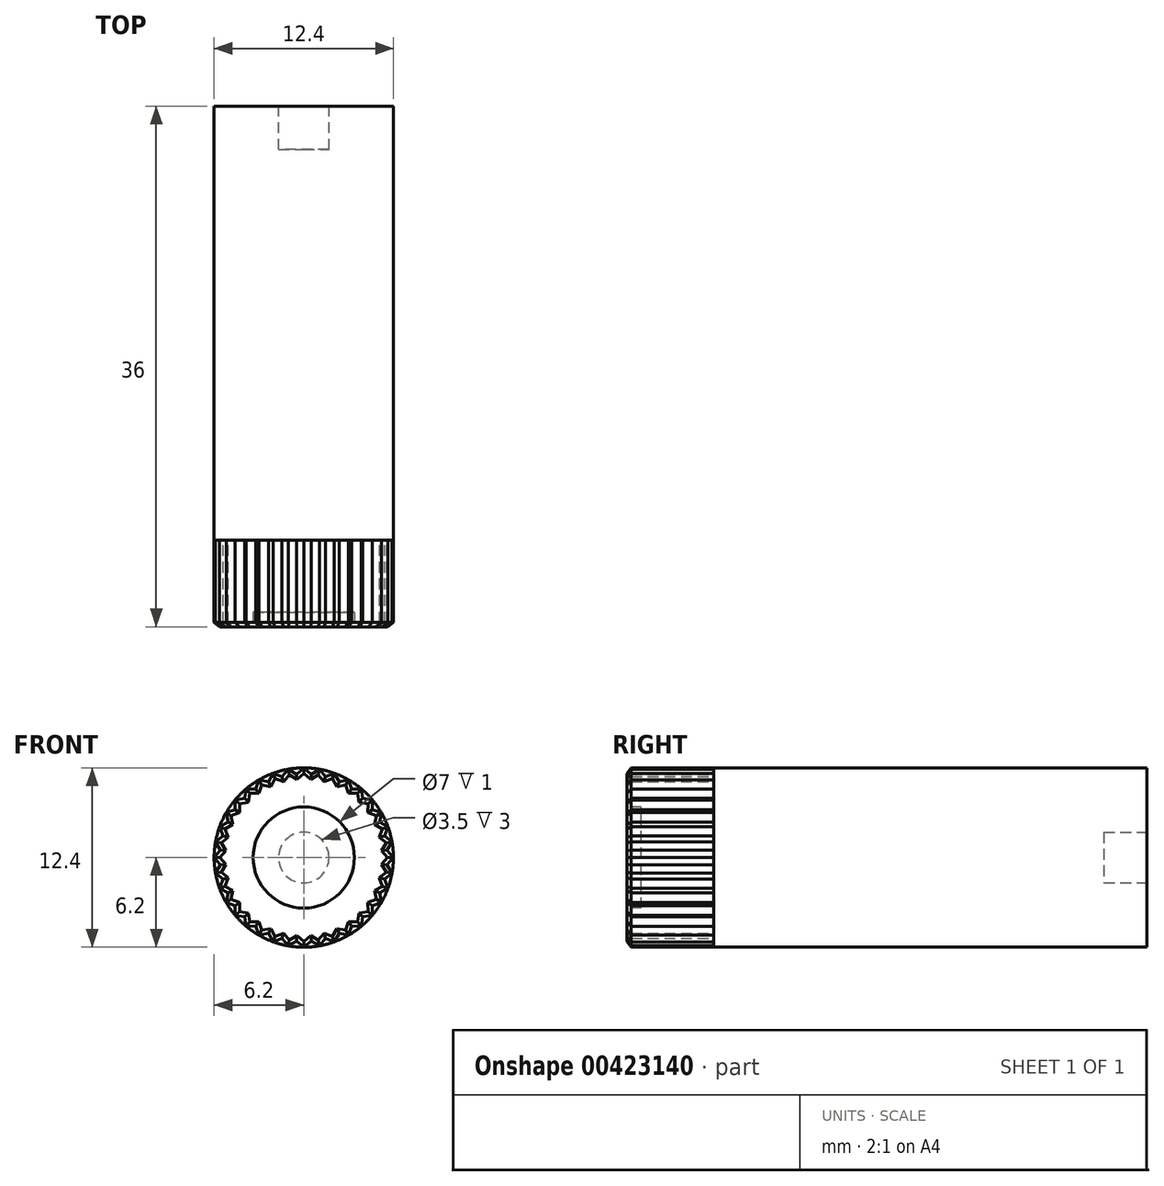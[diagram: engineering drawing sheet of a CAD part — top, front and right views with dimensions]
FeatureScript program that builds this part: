
annotation { "Feature Type Name" : "Feature", "Feature Type Description" : "" }
export const myFeature = defineFeature(function(context is Context, id is Id, definition is map)
    precondition{}
    {
        {
            var Q0;
            Q0=qCreatedBy(makeId("Front.planeOp"),FACE);
            var sketch = newSketch(context, id + "F0", { "sketchPlane" : qUnion([Q0])});
            skCircle(sketch, "E0", {"center": v(0, 0) * mm, "radius": 6.2 * mm});
            skSolve(sketch);
        }
        {
            var Q0;
            Q0 = qSketchRegion(id + "F0", true);
            extrude(context, id + "F1", {"entities" : qUnion([Q0]), "depth" : 30 * mm});
        }
        {
            var Q0;
            Q0=makeQuery(id+"F1.opExtrude","CAP_FACE",FACE,{"disambiguationData":[OSD([sQuery(id+"F0.wireOp",EDGE,"E0")])],"isStart":false});
            var sketch = newSketch(context, id + "F2", { "sketchPlane" : qUnion([Q0])});
            skLineSegment(sketch, "E1", {"start": v(6.2, 0) * mm, "end": v(5.76, 0.5) * mm});
            skLineSegment(sketch, "E2.MirrorCS", {"start": v(6.2, 0) * mm, "end": v(5.76, -0.5) * mm});
            skLineSegment(sketch, "E3.1.0", {"start": v(6.1, 1.08) * mm, "end": v(5.59, 1.5) * mm});
            skLineSegment(sketch, "E3.1.1", {"start": v(6.1, 1.08) * mm, "end": v(5.76, 0.5) * mm});
            skLineSegment(sketch, "E3.2.0", {"start": v(5.83, 2.12) * mm, "end": v(5.24, 2.44) * mm});
            skLineSegment(sketch, "E3.2.1", {"start": v(5.83, 2.12) * mm, "end": v(5.59, 1.5) * mm});
            skLineSegment(sketch, "E3.3.0", {"start": v(5.37, 3.1) * mm, "end": v(4.74, 3.32) * mm});
            skLineSegment(sketch, "E3.3.1", {"start": v(5.37, 3.1) * mm, "end": v(5.24, 2.44) * mm});
            skLineSegment(sketch, "E3.4.0", {"start": v(4.75, 3.99) * mm, "end": v(4.09, 4.09) * mm});
            skLineSegment(sketch, "E3.4.1", {"start": v(4.75, 3.99) * mm, "end": v(4.74, 3.32) * mm});
            skLineSegment(sketch, "E3.5.0", {"start": v(3.99, 4.75) * mm, "end": v(3.32, 4.74) * mm});
            skLineSegment(sketch, "E3.5.1", {"start": v(3.99, 4.75) * mm, "end": v(4.09, 4.09) * mm});
            skLineSegment(sketch, "E3.6.0", {"start": v(3.1, 5.37) * mm, "end": v(2.44, 5.24) * mm});
            skLineSegment(sketch, "E3.6.1", {"start": v(3.1, 5.37) * mm, "end": v(3.32, 4.74) * mm});
            skLineSegment(sketch, "E3.7.0", {"start": v(2.12, 5.83) * mm, "end": v(1.5, 5.59) * mm});
            skLineSegment(sketch, "E3.7.1", {"start": v(2.12, 5.83) * mm, "end": v(2.44, 5.24) * mm});
            skLineSegment(sketch, "E3.8.0", {"start": v(1.08, 6.1) * mm, "end": v(0.5, 5.76) * mm});
            skLineSegment(sketch, "E3.8.1", {"start": v(1.08, 6.1) * mm, "end": v(1.5, 5.59) * mm});
            skLineSegment(sketch, "E3.9.0", {"start": v(0, 6.2) * mm, "end": v(-0.5, 5.76) * mm});
            skLineSegment(sketch, "E3.9.1", {"start": v(0, 6.2) * mm, "end": v(0.5, 5.76) * mm});
            skLineSegment(sketch, "E3.10.0", {"start": v(-1.08, 6.1) * mm, "end": v(-1.5, 5.59) * mm});
            skLineSegment(sketch, "E3.10.1", {"start": v(-1.08, 6.1) * mm, "end": v(-0.5, 5.76) * mm});
            skLineSegment(sketch, "E3.11.0", {"start": v(-2.12, 5.83) * mm, "end": v(-2.44, 5.24) * mm});
            skLineSegment(sketch, "E3.11.1", {"start": v(-2.12, 5.83) * mm, "end": v(-1.5, 5.59) * mm});
            skLineSegment(sketch, "E3.12.0", {"start": v(-3.1, 5.37) * mm, "end": v(-3.32, 4.74) * mm});
            skLineSegment(sketch, "E3.12.1", {"start": v(-3.1, 5.37) * mm, "end": v(-2.44, 5.24) * mm});
            skLineSegment(sketch, "E3.13.0", {"start": v(-3.99, 4.75) * mm, "end": v(-4.09, 4.09) * mm});
            skLineSegment(sketch, "E3.13.1", {"start": v(-3.99, 4.75) * mm, "end": v(-3.32, 4.74) * mm});
            skLineSegment(sketch, "E3.14.0", {"start": v(-4.75, 3.99) * mm, "end": v(-4.74, 3.32) * mm});
            skLineSegment(sketch, "E3.14.1", {"start": v(-4.75, 3.99) * mm, "end": v(-4.09, 4.09) * mm});
            skLineSegment(sketch, "E3.15.0", {"start": v(-5.37, 3.1) * mm, "end": v(-5.24, 2.44) * mm});
            skLineSegment(sketch, "E3.15.1", {"start": v(-5.37, 3.1) * mm, "end": v(-4.74, 3.32) * mm});
            skLineSegment(sketch, "E3.16.0", {"start": v(-5.83, 2.12) * mm, "end": v(-5.59, 1.5) * mm});
            skLineSegment(sketch, "E3.16.1", {"start": v(-5.83, 2.12) * mm, "end": v(-5.24, 2.44) * mm});
            skLineSegment(sketch, "E3.17.0", {"start": v(-6.1, 1.08) * mm, "end": v(-5.76, 0.5) * mm});
            skLineSegment(sketch, "E3.17.1", {"start": v(-6.1, 1.08) * mm, "end": v(-5.59, 1.5) * mm});
            skLineSegment(sketch, "E3.18.0", {"start": v(-6.2, 0) * mm, "end": v(-5.76, -0.5) * mm});
            skLineSegment(sketch, "E3.18.1", {"start": v(-6.2, 0) * mm, "end": v(-5.76, 0.5) * mm});
            skLineSegment(sketch, "E3.19.0", {"start": v(-6.1, -1.08) * mm, "end": v(-5.59, -1.5) * mm});
            skLineSegment(sketch, "E3.19.1", {"start": v(-6.1, -1.08) * mm, "end": v(-5.76, -0.5) * mm});
            skLineSegment(sketch, "E3.20.0", {"start": v(-5.83, -2.12) * mm, "end": v(-5.24, -2.44) * mm});
            skLineSegment(sketch, "E3.20.1", {"start": v(-5.83, -2.12) * mm, "end": v(-5.59, -1.5) * mm});
            skLineSegment(sketch, "E3.21.0", {"start": v(-5.37, -3.1) * mm, "end": v(-4.74, -3.32) * mm});
            skLineSegment(sketch, "E3.21.1", {"start": v(-5.37, -3.1) * mm, "end": v(-5.24, -2.44) * mm});
            skLineSegment(sketch, "E3.22.0", {"start": v(-4.75, -3.99) * mm, "end": v(-4.09, -4.09) * mm});
            skLineSegment(sketch, "E3.22.1", {"start": v(-4.75, -3.99) * mm, "end": v(-4.74, -3.32) * mm});
            skLineSegment(sketch, "E3.23.0", {"start": v(-3.99, -4.75) * mm, "end": v(-3.32, -4.74) * mm});
            skLineSegment(sketch, "E3.23.1", {"start": v(-3.99, -4.75) * mm, "end": v(-4.09, -4.09) * mm});
            skLineSegment(sketch, "E3.24.0", {"start": v(-3.1, -5.37) * mm, "end": v(-2.44, -5.24) * mm});
            skLineSegment(sketch, "E3.24.1", {"start": v(-3.1, -5.37) * mm, "end": v(-3.32, -4.74) * mm});
            skLineSegment(sketch, "E3.25.0", {"start": v(-2.12, -5.83) * mm, "end": v(-1.5, -5.59) * mm});
            skLineSegment(sketch, "E3.25.1", {"start": v(-2.12, -5.83) * mm, "end": v(-2.44, -5.24) * mm});
            skLineSegment(sketch, "E3.26.0", {"start": v(-1.08, -6.1) * mm, "end": v(-0.5, -5.76) * mm});
            skLineSegment(sketch, "E3.26.1", {"start": v(-1.08, -6.1) * mm, "end": v(-1.5, -5.59) * mm});
            skLineSegment(sketch, "E3.27.0", {"start": v(0, -6.2) * mm, "end": v(0.5, -5.76) * mm});
            skLineSegment(sketch, "E3.27.1", {"start": v(0, -6.2) * mm, "end": v(-0.5, -5.76) * mm});
            skLineSegment(sketch, "E3.28.0", {"start": v(1.08, -6.1) * mm, "end": v(1.5, -5.59) * mm});
            skLineSegment(sketch, "E3.28.1", {"start": v(1.08, -6.1) * mm, "end": v(0.5, -5.76) * mm});
            skLineSegment(sketch, "E3.29.0", {"start": v(2.12, -5.83) * mm, "end": v(2.44, -5.24) * mm});
            skLineSegment(sketch, "E3.29.1", {"start": v(2.12, -5.83) * mm, "end": v(1.5, -5.59) * mm});
            skLineSegment(sketch, "E3.30.0", {"start": v(3.1, -5.37) * mm, "end": v(3.32, -4.74) * mm});
            skLineSegment(sketch, "E3.30.1", {"start": v(3.1, -5.37) * mm, "end": v(2.44, -5.24) * mm});
            skLineSegment(sketch, "E3.31.0", {"start": v(3.99, -4.75) * mm, "end": v(4.09, -4.09) * mm});
            skLineSegment(sketch, "E3.31.1", {"start": v(3.99, -4.75) * mm, "end": v(3.32, -4.74) * mm});
            skLineSegment(sketch, "E3.32.0", {"start": v(4.75, -3.99) * mm, "end": v(4.74, -3.32) * mm});
            skLineSegment(sketch, "E3.32.1", {"start": v(4.75, -3.99) * mm, "end": v(4.09, -4.09) * mm});
            skLineSegment(sketch, "E3.33.0", {"start": v(5.37, -3.1) * mm, "end": v(5.24, -2.44) * mm});
            skLineSegment(sketch, "E3.33.1", {"start": v(5.37, -3.1) * mm, "end": v(4.74, -3.32) * mm});
            skLineSegment(sketch, "E3.34.0", {"start": v(5.83, -2.12) * mm, "end": v(5.59, -1.5) * mm});
            skLineSegment(sketch, "E3.34.1", {"start": v(5.83, -2.12) * mm, "end": v(5.24, -2.44) * mm});
            skLineSegment(sketch, "E3.35.0", {"start": v(6.1, -1.08) * mm, "end": v(5.76, -0.5) * mm});
            skLineSegment(sketch, "E3.35.1", {"start": v(6.1, -1.08) * mm, "end": v(5.59, -1.5) * mm});
            skPoint(sketch, "E3.center", {"position": v(0, 0) * mm});
            skSolve(sketch);
        }
        {
            var Q0;
            Q0 = qSketchRegion(id + "F2", true);
            extrude(context, id + "F3", {"entities" : qUnion([Q0]), "operationType" : NewBodyOperationType.ADD, "depth" : 6 * mm});
        }
        {
            var Q0;
            Q0=makeQuery(id+"F3.opExtrude","CAP_FACE",FACE,{"disambiguationData":[OSD([sQuery(id+"F2.wireOp",EDGE,"E1"),sQuery(id+"F2.wireOp",EDGE,"E2.MirrorCS"),sQuery(id+"F2.wireOp",EDGE,"E3.1.0"),sQuery(id+"F2.wireOp",EDGE,"E3.1.1"),sQuery(id+"F2.wireOp",EDGE,"E3.2.0"),sQuery(id+"F2.wireOp",EDGE,"E3.2.1"),sQuery(id+"F2.wireOp",EDGE,"E3.3.0"),sQuery(id+"F2.wireOp",EDGE,"E3.3.1"),sQuery(id+"F2.wireOp",EDGE,"E3.4.0"),sQuery(id+"F2.wireOp",EDGE,"E3.4.1"),sQuery(id+"F2.wireOp",EDGE,"E3.5.0"),sQuery(id+"F2.wireOp",EDGE,"E3.5.1"),sQuery(id+"F2.wireOp",EDGE,"E3.6.0"),sQuery(id+"F2.wireOp",EDGE,"E3.6.1"),sQuery(id+"F2.wireOp",EDGE,"E3.7.0"),sQuery(id+"F2.wireOp",EDGE,"E3.7.1"),sQuery(id+"F2.wireOp",EDGE,"E3.8.0"),sQuery(id+"F2.wireOp",EDGE,"E3.8.1"),sQuery(id+"F2.wireOp",EDGE,"E3.9.0"),sQuery(id+"F2.wireOp",EDGE,"E3.9.1"),sQuery(id+"F2.wireOp",EDGE,"E3.10.0"),sQuery(id+"F2.wireOp",EDGE,"E3.10.1"),sQuery(id+"F2.wireOp",EDGE,"E3.11.0"),sQuery(id+"F2.wireOp",EDGE,"E3.11.1"),sQuery(id+"F2.wireOp",EDGE,"E3.12.0"),sQuery(id+"F2.wireOp",EDGE,"E3.12.1"),sQuery(id+"F2.wireOp",EDGE,"E3.13.0"),sQuery(id+"F2.wireOp",EDGE,"E3.13.1"),sQuery(id+"F2.wireOp",EDGE,"E3.14.0"),sQuery(id+"F2.wireOp",EDGE,"E3.14.1"),sQuery(id+"F2.wireOp",EDGE,"E3.15.0"),sQuery(id+"F2.wireOp",EDGE,"E3.15.1"),sQuery(id+"F2.wireOp",EDGE,"E3.16.0"),sQuery(id+"F2.wireOp",EDGE,"E3.16.1"),sQuery(id+"F2.wireOp",EDGE,"E3.17.0"),sQuery(id+"F2.wireOp",EDGE,"E3.17.1"),sQuery(id+"F2.wireOp",EDGE,"E3.18.0"),sQuery(id+"F2.wireOp",EDGE,"E3.18.1"),sQuery(id+"F2.wireOp",EDGE,"E3.19.0"),sQuery(id+"F2.wireOp",EDGE,"E3.19.1"),sQuery(id+"F2.wireOp",EDGE,"E3.20.0"),sQuery(id+"F2.wireOp",EDGE,"E3.20.1"),sQuery(id+"F2.wireOp",EDGE,"E3.21.0"),sQuery(id+"F2.wireOp",EDGE,"E3.21.1"),sQuery(id+"F2.wireOp",EDGE,"E3.22.0"),sQuery(id+"F2.wireOp",EDGE,"E3.22.1"),sQuery(id+"F2.wireOp",EDGE,"E3.23.0"),sQuery(id+"F2.wireOp",EDGE,"E3.23.1"),sQuery(id+"F2.wireOp",EDGE,"E3.24.0"),sQuery(id+"F2.wireOp",EDGE,"E3.24.1"),sQuery(id+"F2.wireOp",EDGE,"E3.25.0"),sQuery(id+"F2.wireOp",EDGE,"E3.25.1"),sQuery(id+"F2.wireOp",EDGE,"E3.26.0"),sQuery(id+"F2.wireOp",EDGE,"E3.26.1"),sQuery(id+"F2.wireOp",EDGE,"E3.27.0"),sQuery(id+"F2.wireOp",EDGE,"E3.27.1"),sQuery(id+"F2.wireOp",EDGE,"E3.28.0"),sQuery(id+"F2.wireOp",EDGE,"E3.28.1"),sQuery(id+"F2.wireOp",EDGE,"E3.29.0"),sQuery(id+"F2.wireOp",EDGE,"E3.29.1"),sQuery(id+"F2.wireOp",EDGE,"E3.30.0"),sQuery(id+"F2.wireOp",EDGE,"E3.30.1"),sQuery(id+"F2.wireOp",EDGE,"E3.31.0"),sQuery(id+"F2.wireOp",EDGE,"E3.31.1"),sQuery(id+"F2.wireOp",EDGE,"E3.32.0"),sQuery(id+"F2.wireOp",EDGE,"E3.32.1"),sQuery(id+"F2.wireOp",EDGE,"E3.33.0"),sQuery(id+"F2.wireOp",EDGE,"E3.33.1"),sQuery(id+"F2.wireOp",EDGE,"E3.34.0"),sQuery(id+"F2.wireOp",EDGE,"E3.34.1"),sQuery(id+"F2.wireOp",EDGE,"E3.35.0"),sQuery(id+"F2.wireOp",EDGE,"E3.35.1")])],"isStart":false});
            chamfer(context, id + "F4", {"entities" : qUnion([Q0]), "width" : 0.3 * mm, "tangentPropagation" : true});
        }
        {
            var Q0;
            Q0=makeQuery(id+"F3.opExtrude","CAP_FACE",FACE,{"disambiguationData":[OSD([sQuery(id+"F2.wireOp",EDGE,"E1"),sQuery(id+"F2.wireOp",EDGE,"E2.MirrorCS"),sQuery(id+"F2.wireOp",EDGE,"E3.1.0"),sQuery(id+"F2.wireOp",EDGE,"E3.1.1"),sQuery(id+"F2.wireOp",EDGE,"E3.2.0"),sQuery(id+"F2.wireOp",EDGE,"E3.2.1"),sQuery(id+"F2.wireOp",EDGE,"E3.3.0"),sQuery(id+"F2.wireOp",EDGE,"E3.3.1"),sQuery(id+"F2.wireOp",EDGE,"E3.4.0"),sQuery(id+"F2.wireOp",EDGE,"E3.4.1"),sQuery(id+"F2.wireOp",EDGE,"E3.5.0"),sQuery(id+"F2.wireOp",EDGE,"E3.5.1"),sQuery(id+"F2.wireOp",EDGE,"E3.6.0"),sQuery(id+"F2.wireOp",EDGE,"E3.6.1"),sQuery(id+"F2.wireOp",EDGE,"E3.7.0"),sQuery(id+"F2.wireOp",EDGE,"E3.7.1"),sQuery(id+"F2.wireOp",EDGE,"E3.8.0"),sQuery(id+"F2.wireOp",EDGE,"E3.8.1"),sQuery(id+"F2.wireOp",EDGE,"E3.9.0"),sQuery(id+"F2.wireOp",EDGE,"E3.9.1"),sQuery(id+"F2.wireOp",EDGE,"E3.10.0"),sQuery(id+"F2.wireOp",EDGE,"E3.10.1"),sQuery(id+"F2.wireOp",EDGE,"E3.11.0"),sQuery(id+"F2.wireOp",EDGE,"E3.11.1"),sQuery(id+"F2.wireOp",EDGE,"E3.12.0"),sQuery(id+"F2.wireOp",EDGE,"E3.12.1"),sQuery(id+"F2.wireOp",EDGE,"E3.13.0"),sQuery(id+"F2.wireOp",EDGE,"E3.13.1"),sQuery(id+"F2.wireOp",EDGE,"E3.14.0"),sQuery(id+"F2.wireOp",EDGE,"E3.14.1"),sQuery(id+"F2.wireOp",EDGE,"E3.15.0"),sQuery(id+"F2.wireOp",EDGE,"E3.15.1"),sQuery(id+"F2.wireOp",EDGE,"E3.16.0"),sQuery(id+"F2.wireOp",EDGE,"E3.16.1"),sQuery(id+"F2.wireOp",EDGE,"E3.17.0"),sQuery(id+"F2.wireOp",EDGE,"E3.17.1"),sQuery(id+"F2.wireOp",EDGE,"E3.18.0"),sQuery(id+"F2.wireOp",EDGE,"E3.18.1"),sQuery(id+"F2.wireOp",EDGE,"E3.19.0"),sQuery(id+"F2.wireOp",EDGE,"E3.19.1"),sQuery(id+"F2.wireOp",EDGE,"E3.20.0"),sQuery(id+"F2.wireOp",EDGE,"E3.20.1"),sQuery(id+"F2.wireOp",EDGE,"E3.21.0"),sQuery(id+"F2.wireOp",EDGE,"E3.21.1"),sQuery(id+"F2.wireOp",EDGE,"E3.22.0"),sQuery(id+"F2.wireOp",EDGE,"E3.22.1"),sQuery(id+"F2.wireOp",EDGE,"E3.23.0"),sQuery(id+"F2.wireOp",EDGE,"E3.23.1"),sQuery(id+"F2.wireOp",EDGE,"E3.24.0"),sQuery(id+"F2.wireOp",EDGE,"E3.24.1"),sQuery(id+"F2.wireOp",EDGE,"E3.25.0"),sQuery(id+"F2.wireOp",EDGE,"E3.25.1"),sQuery(id+"F2.wireOp",EDGE,"E3.26.0"),sQuery(id+"F2.wireOp",EDGE,"E3.26.1"),sQuery(id+"F2.wireOp",EDGE,"E3.27.0"),sQuery(id+"F2.wireOp",EDGE,"E3.27.1"),sQuery(id+"F2.wireOp",EDGE,"E3.28.0"),sQuery(id+"F2.wireOp",EDGE,"E3.28.1"),sQuery(id+"F2.wireOp",EDGE,"E3.29.0"),sQuery(id+"F2.wireOp",EDGE,"E3.29.1"),sQuery(id+"F2.wireOp",EDGE,"E3.30.0"),sQuery(id+"F2.wireOp",EDGE,"E3.30.1"),sQuery(id+"F2.wireOp",EDGE,"E3.31.0"),sQuery(id+"F2.wireOp",EDGE,"E3.31.1"),sQuery(id+"F2.wireOp",EDGE,"E3.32.0"),sQuery(id+"F2.wireOp",EDGE,"E3.32.1"),sQuery(id+"F2.wireOp",EDGE,"E3.33.0"),sQuery(id+"F2.wireOp",EDGE,"E3.33.1"),sQuery(id+"F2.wireOp",EDGE,"E3.34.0"),sQuery(id+"F2.wireOp",EDGE,"E3.34.1"),sQuery(id+"F2.wireOp",EDGE,"E3.35.0"),sQuery(id+"F2.wireOp",EDGE,"E3.35.1")])],"isStart":false});
            var sketch = newSketch(context, id + "F5", { "sketchPlane" : qUnion([Q0])});
            skCircle(sketch, "E4", {"center": v(0, 0) * mm, "radius": 3.5 * mm});
            skSolve(sketch);
        }
        {
            var Q0;
            Q0 = qSketchRegion(id + "F5", true);
            extrude(context, id + "F6", {"entities" : qUnion([Q0]), "operationType" : NewBodyOperationType.REMOVE, "oppositeDirection" : true, "depth" : 1 * mm});
        }
        {
            var Q0;
            Q0=makeQuery(id+"F1.opExtrude","CAP_FACE",FACE,{"disambiguationData":[OSD([sQuery(id+"F0.wireOp",EDGE,"E0")])],"isStart":true});
            var sketch = newSketch(context, id + "F7", { "sketchPlane" : qUnion([Q0])});
            skCircle(sketch, "E5", {"center": v(0, 0) * mm, "radius": 1.75 * mm});
            skSolve(sketch);
        }
        {
            var Q0;
            Q0 = qSketchRegion(id + "F7", true);
            extrude(context, id + "F8", {"entities" : qUnion([Q0]), "operationType" : NewBodyOperationType.REMOVE, "oppositeDirection" : true, "depth" : 3 * mm});
        }
    });
